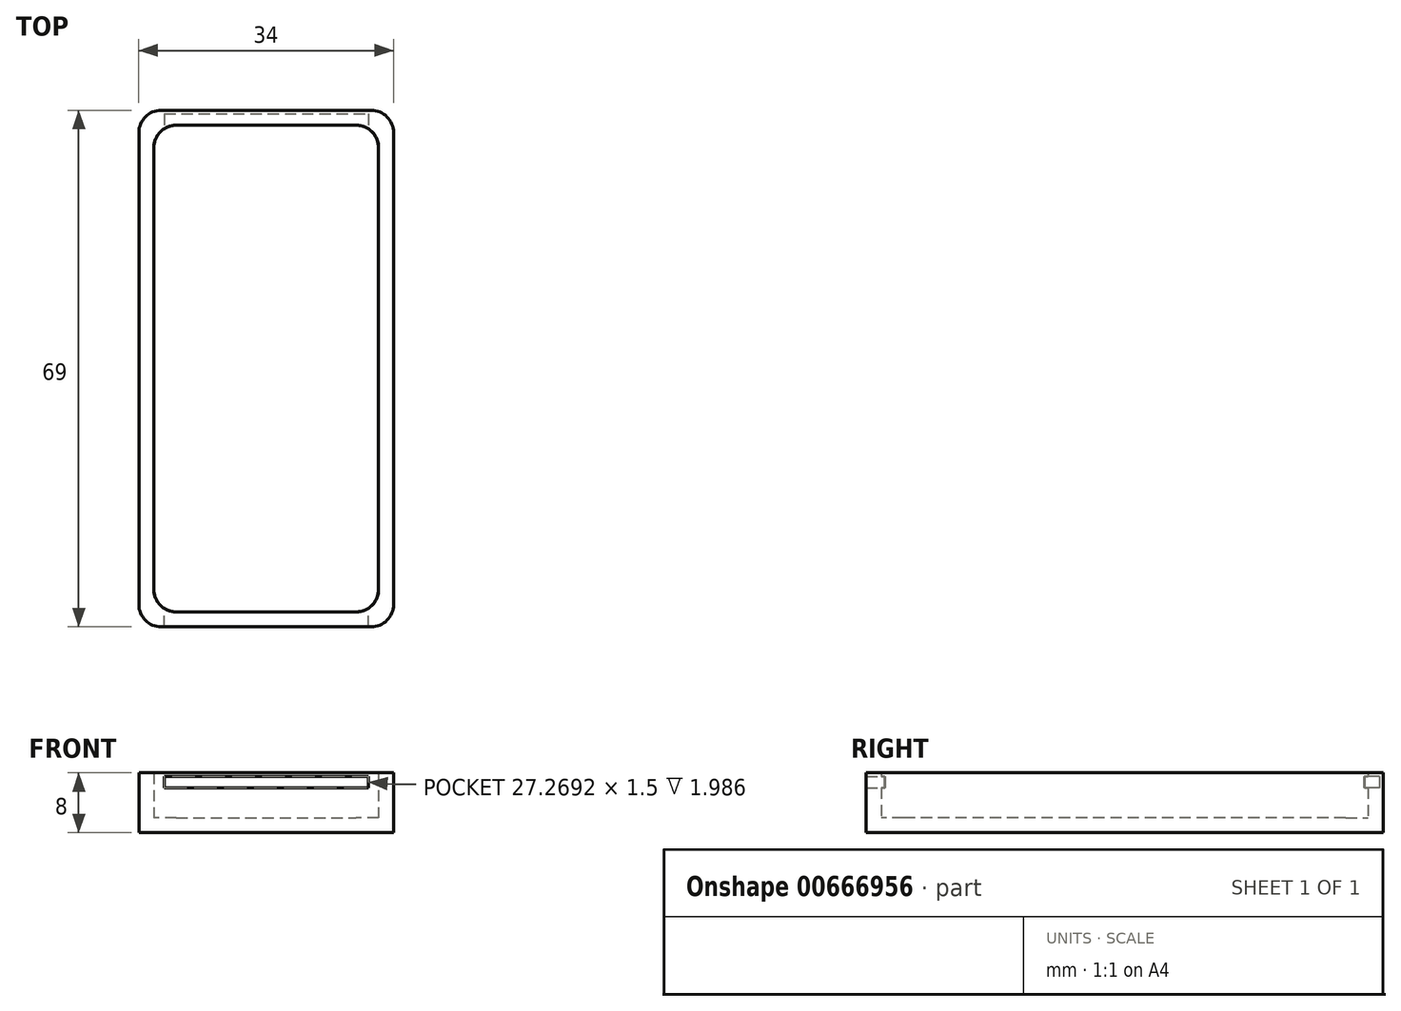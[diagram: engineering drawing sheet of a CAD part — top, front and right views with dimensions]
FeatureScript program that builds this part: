
annotation { "Feature Type Name" : "Feature", "Feature Type Description" : "" }
export const myFeature = defineFeature(function(context is Context, id is Id, definition is map)
    precondition{}
    {
        {
            var Q0;
            Q0=qCreatedBy(makeId("Top.planeOp"),FACE);
            var sketch = newSketch(context, id + "F0", { "sketchPlane" : qUnion([Q0])});
            skLineSegment(sketch, "E0.bottom", {"start": v(-13.67, 43.88) * mm, "end": v(16.33, 43.88) * mm});
            skLineSegment(sketch, "E0.top", {"start": v(-13.67, -21.12) * mm, "end": v(16.33, -21.12) * mm});
            skLineSegment(sketch, "E0.left", {"start": v(-13.67, 43.88) * mm, "end": v(-13.67, -21.12) * mm});
            skLineSegment(sketch, "E0.right", {"start": v(16.33, 43.88) * mm, "end": v(16.33, -21.12) * mm});
            skSolve(sketch);
        }
        {
            var Q0;
            Q0=makeQuery(id+"F0.imprint","IMPRINT",FACE,{"disambiguationData":[TD([[makeQuery(id+"F0.imprint","IMPRINT",EDGE,{"derivedFrom":sQuery(id+"F0.wireOp",EDGE,"E0.bottom")}),-1.0]])]});
            var sketch = newSketch(context, id + "F1", { "sketchPlane" : qUnion([Q0])});
            skLineSegment(sketch, "E1.0", {"start": v(-15.67, 45.88) * mm, "end": v(-15.67, -23.12) * mm});
            skLineSegment(sketch, "E1.1", {"start": v(18.33, 45.88) * mm, "end": v(-15.67, 45.88) * mm});
            skLineSegment(sketch, "E1.2", {"start": v(18.33, -23.12) * mm, "end": v(18.33, 45.88) * mm});
            skLineSegment(sketch, "E1.3", {"start": v(-15.67, -23.12) * mm, "end": v(18.33, -23.12) * mm});
            skSolve(sketch);
        }
        {
            var Q0;
            Q0=makeQuery(id+"F1.imprint","IMPRINT",FACE,{"disambiguationData":[TD([[makeQuery(id+"F1.imprint","IMPRINT",EDGE,{"derivedFrom":sQuery(id+"F1.wireOp",EDGE,"E1.0")}),1.0]])]});
            extrude(context, id + "F2", {"entities" : qUnion([Q0]), "depth" : 8 * mm, "offsetDistance" : 25 * mm});
        }
        {
            var Q0;
            Q0 = qSketchRegion(id + "F1", true);
            extrude(context, id + "F3", {"entities" : qUnion([Q0]), "operationType" : NewBodyOperationType.ADD, "depth" : 2 * mm, "offsetDistance" : 25 * mm});
        }
        {
            var Q0;
            Q0=makeQuery(id+"F2.opExtrude","SWEPT_EDGE",EDGE,{"disambiguationData":[OSD([sQuery(id+"F1.wireOp",EDGE,"E1.0"),sQuery(id+"F1.wireOp",EDGE,"E1.1")])]});
            var Q1;
            Q1=makeQuery(id+"F2.opExtrude","SWEPT_EDGE",EDGE,{"disambiguationData":[OSD([sQuery(id+"F1.wireOp",EDGE,"E1.1"),sQuery(id+"F1.wireOp",EDGE,"E1.2")])]});
            var Q2;
            Q2=makeQuery(id+"F2.opExtrude","SWEPT_EDGE",EDGE,{"disambiguationData":[OSD([sQuery(id+"F1.wireOp",EDGE,"E1.2"),sQuery(id+"F1.wireOp",EDGE,"E1.3")])]});
            var Q3;
            Q3=makeQuery(id+"F2.opExtrude","SWEPT_EDGE",EDGE,{"disambiguationData":[OSD([sQuery(id+"F1.wireOp",EDGE,"E1.0"),sQuery(id+"F1.wireOp",EDGE,"E1.3")])]});
            var Q4;
            Q4=makeQuery(id+"F2.opExtrude","SWEPT_EDGE",EDGE,{"disambiguationData":[OSD([sQuery(id+"F0.wireOp",EDGE,"E0.bottom"),sQuery(id+"F0.wireOp",EDGE,"E0.left")])]});
            var Q5;
            Q5=makeQuery(id+"F2.opExtrude","SWEPT_EDGE",EDGE,{"disambiguationData":[OSD([sQuery(id+"F0.wireOp",EDGE,"E0.bottom"),sQuery(id+"F0.wireOp",EDGE,"E0.right")])]});
            var Q6;
            Q6=makeQuery(id+"F2.opExtrude","SWEPT_EDGE",EDGE,{"disambiguationData":[OSD([sQuery(id+"F0.wireOp",EDGE,"E0.top"),sQuery(id+"F0.wireOp",EDGE,"E0.right")])]});
            var Q7;
            Q7=makeQuery(id+"F2.opExtrude","SWEPT_EDGE",EDGE,{"disambiguationData":[OSD([sQuery(id+"F0.wireOp",EDGE,"E0.top"),sQuery(id+"F0.wireOp",EDGE,"E0.left")])]});
            fillet(context, id + "F4", {"entities" : qUnion([Q0, Q1, Q2, Q3, Q4, Q5, Q6, Q7]), "radius" : 3 * mm, "tangentPropagation" : true, "allowEdgeOverflow" : false});
        }
        {
            var Q0;
            Q0=qCreatedBy(makeId("Front.planeOp"),FACE);
            var sketch = newSketch(context, id + "F5", { "sketchPlane" : qUnion([Q0])});
            skLineSegment(sketch, "E2.bottom", {"start": v(-12.27, 7.51) * mm, "end": v(15, 7.51) * mm});
            skLineSegment(sketch, "E2.top", {"start": v(-12.27, 6.01) * mm, "end": v(15, 6.01) * mm});
            skLineSegment(sketch, "E2.left", {"start": v(-12.27, 7.51) * mm, "end": v(-12.27, 6.01) * mm});
            skLineSegment(sketch, "E2.right", {"start": v(15, 7.51) * mm, "end": v(15, 6.01) * mm});
            skSolve(sketch);
        }
        {
            var Q0;
            Q0 = qSketchRegion(id + "F5", true);
            extrude(context, id + "F6", {"entities" : qUnion([Q0]), "operationType" : NewBodyOperationType.REMOVE, "depth" : 25 * mm, "offsetDistance" : 25 * mm});
        }
        {
            var Q0;
            Q0 = qSketchRegion(id + "F5", true);
            extrude(context, id + "F7", {"entities" : qUnion([Q0]), "operationType" : NewBodyOperationType.REMOVE, "oppositeDirection" : true, "depth" : 45.4 * mm, "offsetDistance" : 25 * mm});
        }
    });
